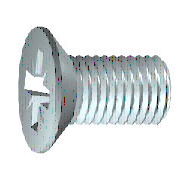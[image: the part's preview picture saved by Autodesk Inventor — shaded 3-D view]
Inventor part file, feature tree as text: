
AUTODESK INVENTOR PART (.ipt)
format: ipt  version: 2021.4 (Build 254397000, 397)  size: 290,304 bytes
history: native  units: mm (DEFAULTED — no unit token found)
features: sketch x3, extrude x2, plane x1
ambient origin geometry x7: Origin, YZ Plane, XZ Plane, X Axis, Y Axis, Z Axis, Center Point
bodies: Solid1 (feature_tree), Body (feature_tree)
feature tree (6):
  sketch  "Sketch1"  dims[d1=4.7mm d2=6.0mm]
  extrude  "Slot"  Depth=6.0mm
  extrude  "Star Cut"  Depth=6.6mm
  plane  "Work Plane2"
  sketch  "Sketch3"  dims[d5=4.625123mm d6=10.821041mm d7=3.45mm d8=0.61345mm d16=90.0deg d9=6.6mm d10=45.0deg d11=0.71mm d12=3.3mm d13=-5.235988mm d14=4.7mm d15=0.0mm d18=11.3mm d19=45.0deg d21=10.0mm d22=2.64mm d23=3.3mm d24=6.6mm d25=45.0deg d26=0.71mm d79=25.4mm d27=0.872665mm d28=0.284mm d29=3.3mm d30=0.0mm d32=0.61345mm d33=0.61355mm d87=45.0deg d91=0.0mm d92=0.0mm]
  sketch  "Sketch2"  dims[d3=5.38655mm d4=6.6mm]
